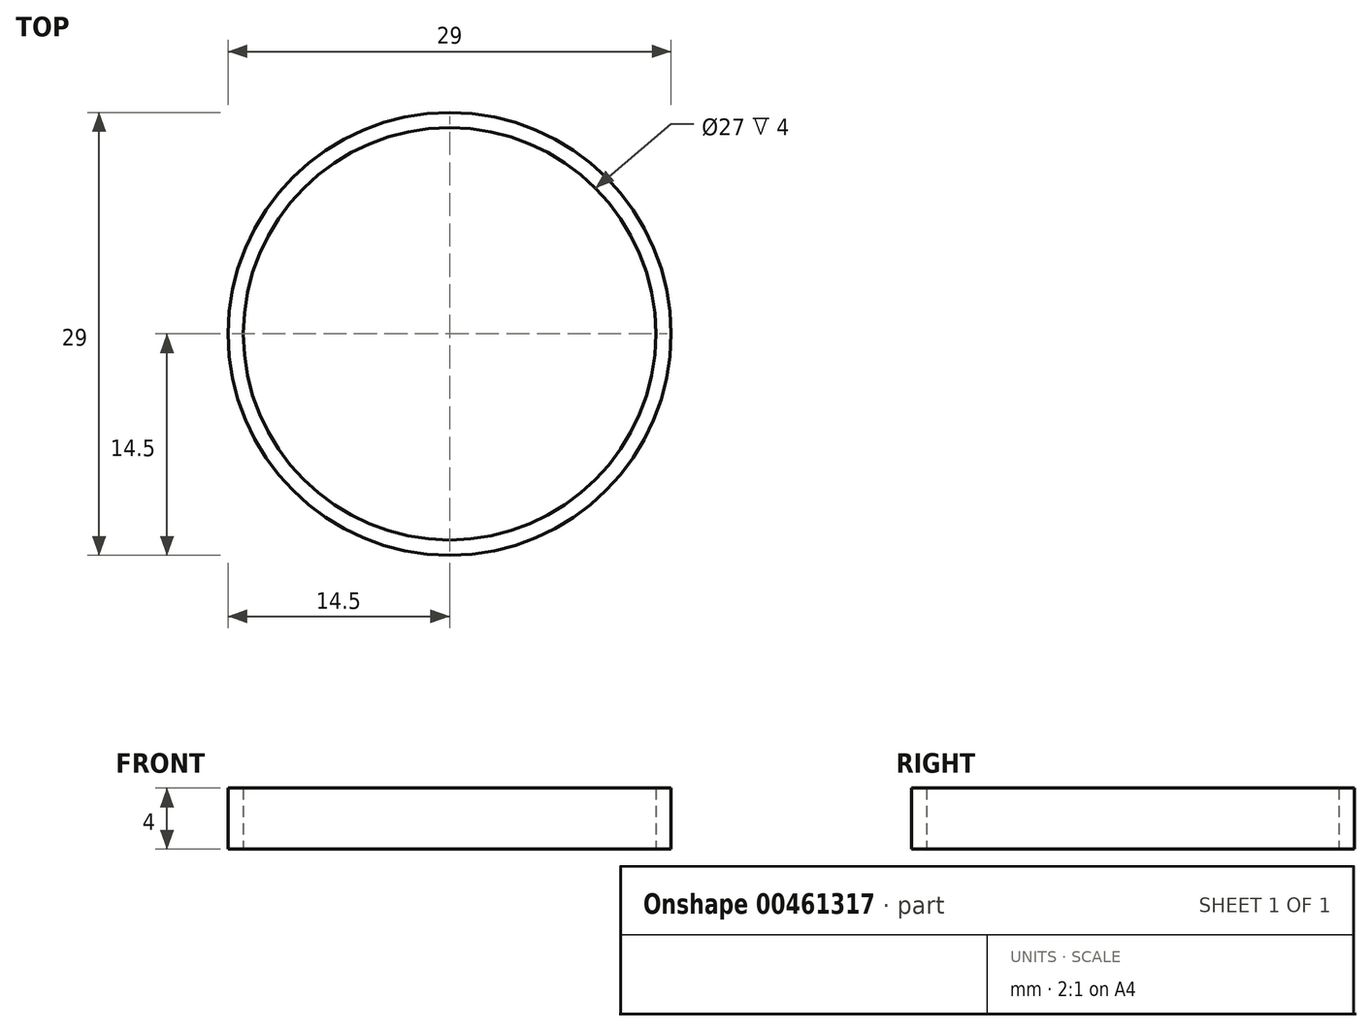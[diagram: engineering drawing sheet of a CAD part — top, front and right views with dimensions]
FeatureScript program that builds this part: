
annotation { "Feature Type Name" : "Feature", "Feature Type Description" : "" }
export const myFeature = defineFeature(function(context is Context, id is Id, definition is map)
    precondition{}
    {
        {
            var Q0;
            Q0=qCreatedBy(makeId("Top.planeOp"),FACE);
            var sketch = newSketch(context, id + "F0", { "sketchPlane" : qUnion([Q0])});
            skCircle(sketch, "E0", {"center": v(0, 0) * mm, "radius": 13.25 * mm});
            skCircle(sketch, "E1", {"center": v(0, 0) * mm, "radius": 13.5 * mm});
            skCircle(sketch, "E2", {"center": v(0, 0) * mm, "radius": 14.5 * mm});
            skSolve(sketch);
        }
        {
            var Q0;
            Q0 = qSketchRegion(id + "F0", true);
            extrude(context, id + "F1", {"entities" : qUnion([Q0]), "depth" : 4 * mm});
        }
    });
